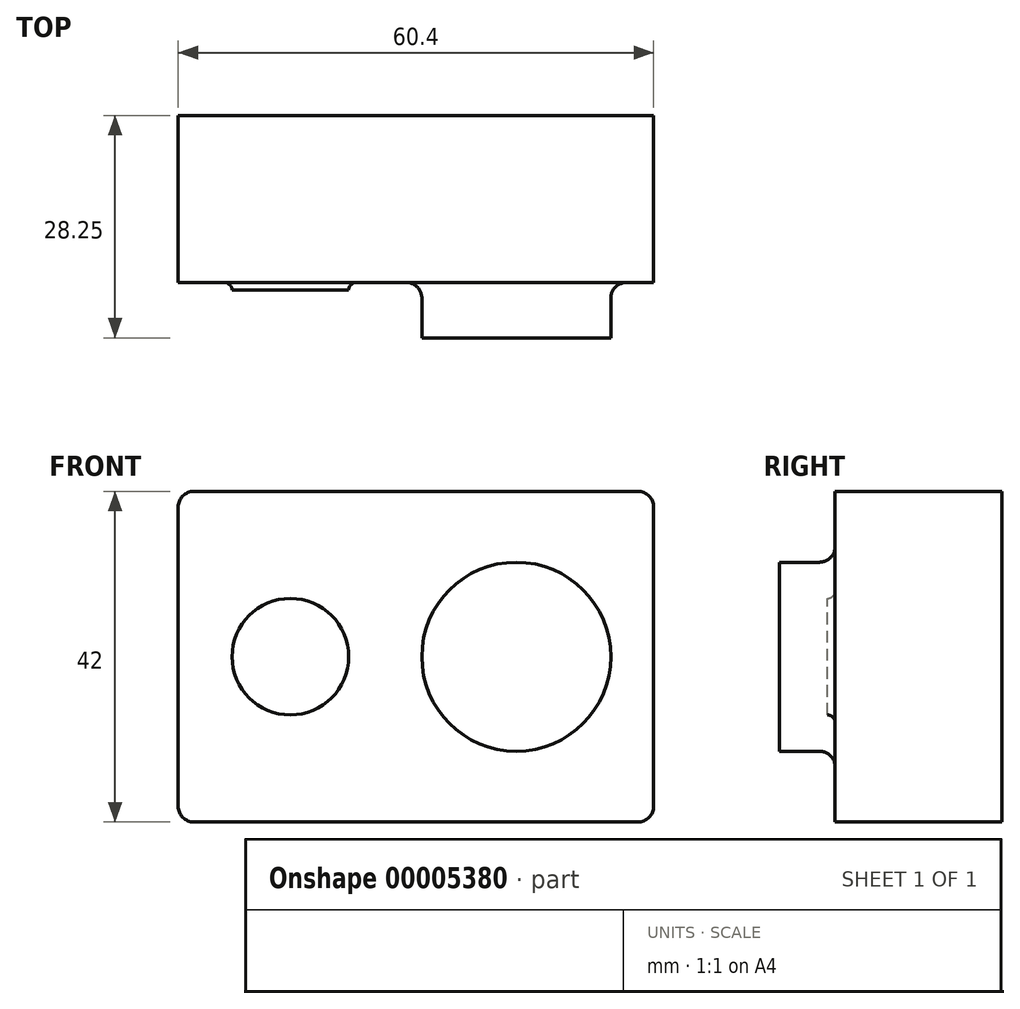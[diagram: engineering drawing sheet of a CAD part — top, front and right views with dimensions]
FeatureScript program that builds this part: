
annotation { "Feature Type Name" : "Feature", "Feature Type Description" : "" }
export const myFeature = defineFeature(function(context is Context, id is Id, definition is map)
    precondition{}
    {
        {
            var Q0;
            Q0=qCreatedBy(makeId("Front.planeOp"),FACE);
            var sketch = newSketch(context, id + "F0", { "sketchPlane" : qUnion([Q0])});
            skLineSegment(sketch, "E0.bottom", {"start": v(-58.77, 31.32) * mm, "end": v(1.63, 31.32) * mm});
            skLineSegment(sketch, "E0.top", {"start": v(-58.77, -10.68) * mm, "end": v(1.63, -10.68) * mm});
            skLineSegment(sketch, "E0.left", {"start": v(-58.77, 31.32) * mm, "end": v(-58.77, -10.68) * mm});
            skLineSegment(sketch, "E0.right", {"start": v(1.63, 31.32) * mm, "end": v(1.63, -10.68) * mm});
            skCircle(sketch, "E1", {"center": v(-44.52, 10.32) * mm, "radius": 7.4 * mm});
            skCircle(sketch, "E2", {"center": v(-15.82, 10.32) * mm, "radius": 12 * mm});
            skSolve(sketch);
        }
        {
            var Q0;
            Q0=makeQuery(id+"F0.imprint","IMPRINT",FACE,{"disambiguationData":[TD([[makeQuery(id+"F0.imprint","IMPRINT",EDGE,{"derivedFrom":sQuery(id+"F0.wireOp",EDGE,"E0.bottom")}),-1.0]])]});
            var Q1;
            Q1=makeQuery(id+"F0.imprint","IMPRINT",FACE,{"disambiguationData":[TD([[makeQuery(id+"F0.imprint","IMPRINT",EDGE,{"derivedFrom":sQuery(id+"F0.wireOp",EDGE,"E1")}),1.0]])]});
            var Q2;
            Q2=makeQuery(id+"F0.imprint","IMPRINT",FACE,{"disambiguationData":[TD([[makeQuery(id+"F0.imprint","IMPRINT",EDGE,{"derivedFrom":sQuery(id+"F0.wireOp",EDGE,"E2")}),1.0]])]});
            extrude(context, id + "F1", {"entities" : qUnion([Q0, Q1, Q2]), "depth" : 21.2 * mm});
        }
        {
            var Q0;
            Q0=makeQuery(id+"F0.imprint","IMPRINT",FACE,{"disambiguationData":[TD([[makeQuery(id+"F0.imprint","IMPRINT",EDGE,{"derivedFrom":sQuery(id+"F0.wireOp",EDGE,"E1")}),1.0]])]});
            extrude(context, id + "F2", {"entities" : qUnion([Q0]), "operationType" : NewBodyOperationType.ADD, "depth" : 22.2 * mm});
        }
        {
            var Q0;
            Q0=makeQuery(id+"F0.imprint","IMPRINT",FACE,{"disambiguationData":[TD([[makeQuery(id+"F0.imprint","IMPRINT",EDGE,{"derivedFrom":sQuery(id+"F0.wireOp",EDGE,"E2")}),1.0]])]});
            extrude(context, id + "F3", {"entities" : qUnion([Q0]), "operationType" : NewBodyOperationType.ADD, "depth" : 28.25 * mm});
        }
        {
            var Q0;
            Q0=makeQuery(id+"F2.boolean.opBoolean","INTERSECT",EDGE,{"derivedFrom":[makeQuery(id+"F1.opExtrude","CAP_FACE",FACE,{"disambiguationData":[OSD([sQuery(id+"F0.wireOp",EDGE,"E0.bottom"),sQuery(id+"F0.wireOp",EDGE,"E0.top"),sQuery(id+"F0.wireOp",EDGE,"E0.left"),sQuery(id+"F0.wireOp",EDGE,"E0.right")])],"isStart":false}),makeQuery(id+"F2.opExtrude","SWEPT_FACE",FACE,{"disambiguationData":[OSD([sQuery(id+"F0.wireOp",EDGE,"E1")])]})]});
            fillet(context, id + "F4", {"entities" : qUnion([Q0]), "radius" : 1 * mm, "tangentPropagation" : true, "allowEdgeOverflow" : false});
        }
        {
            var Q0;
            Q0=makeQuery(id+"F3.boolean.opBoolean","INTERSECT",EDGE,{"derivedFrom":[makeQuery(id+"F1.opExtrude","CAP_FACE",FACE,{"disambiguationData":[OSD([sQuery(id+"F0.wireOp",EDGE,"E0.bottom"),sQuery(id+"F0.wireOp",EDGE,"E0.top"),sQuery(id+"F0.wireOp",EDGE,"E0.left"),sQuery(id+"F0.wireOp",EDGE,"E0.right")])],"isStart":false}),makeQuery(id+"F3.opExtrude","SWEPT_FACE",FACE,{"disambiguationData":[OSD([sQuery(id+"F0.wireOp",EDGE,"E2")])]})]});
            fillet(context, id + "F5", {"entities" : qUnion([Q0]), "radius" : 2 * mm, "tangentPropagation" : true, "allowEdgeOverflow" : false});
        }
        {
            var Q0;
            Q0=makeQuery(id+"F1.opExtrude","SWEPT_EDGE",EDGE,{"disambiguationData":[OSD([sQuery(id+"F0.wireOp",EDGE,"E0.bottom"),sQuery(id+"F0.wireOp",EDGE,"E0.left")])]});
            var Q1;
            Q1=makeQuery(id+"F1.opExtrude","SWEPT_EDGE",EDGE,{"disambiguationData":[OSD([sQuery(id+"F0.wireOp",EDGE,"E0.bottom"),sQuery(id+"F0.wireOp",EDGE,"E0.right")])]});
            var Q2;
            Q2=makeQuery(id+"F1.opExtrude","SWEPT_EDGE",EDGE,{"disambiguationData":[OSD([sQuery(id+"F0.wireOp",EDGE,"E0.top"),sQuery(id+"F0.wireOp",EDGE,"E0.right")])]});
            var Q3;
            Q3=makeQuery(id+"F1.opExtrude","SWEPT_EDGE",EDGE,{"disambiguationData":[OSD([sQuery(id+"F0.wireOp",EDGE,"E0.top"),sQuery(id+"F0.wireOp",EDGE,"E0.left")])]});
            fillet(context, id + "F6", {"entities" : qUnion([Q0, Q1, Q2, Q3]), "radius" : 2 * mm, "tangentPropagation" : true, "allowEdgeOverflow" : false});
        }
    });
